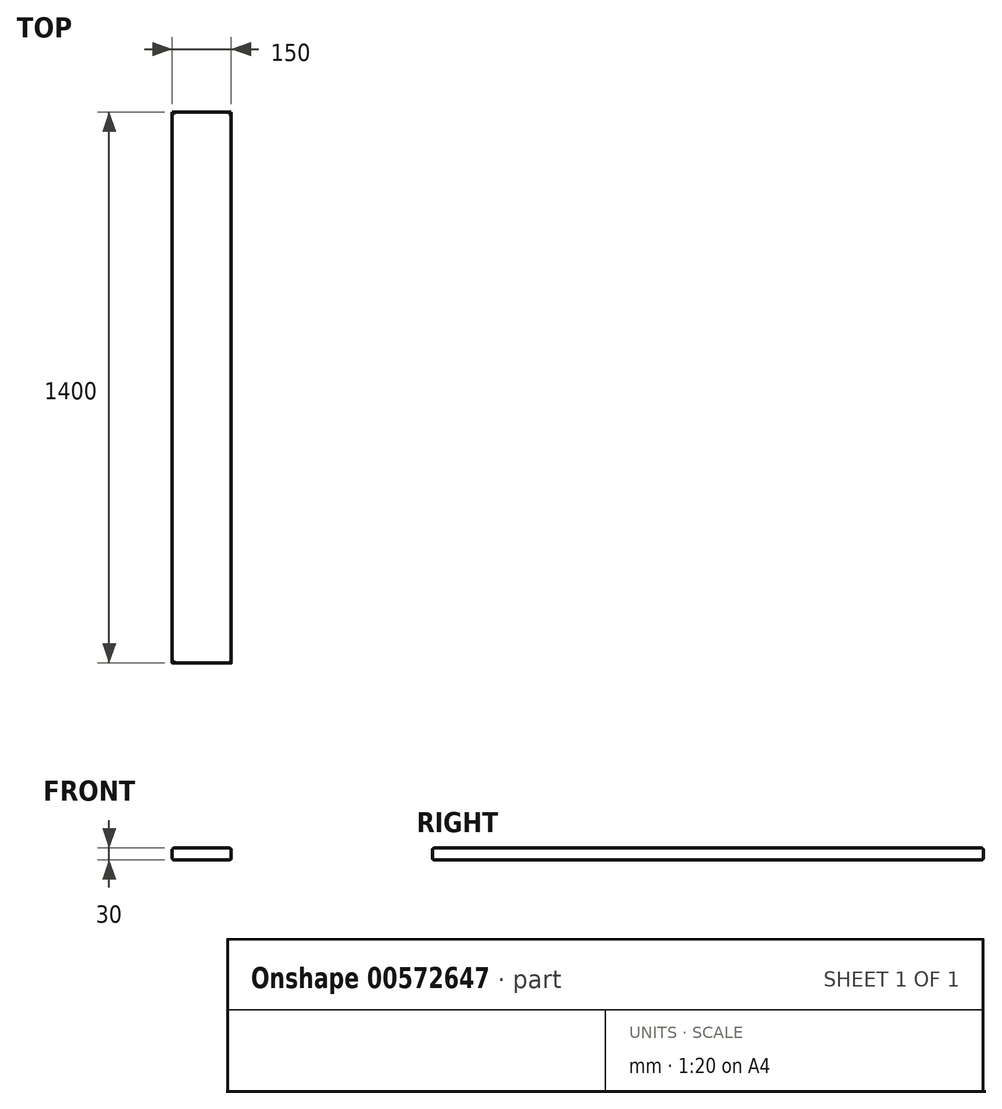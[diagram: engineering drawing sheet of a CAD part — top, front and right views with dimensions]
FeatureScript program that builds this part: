
annotation { "Feature Type Name" : "Feature", "Feature Type Description" : "" }
export const myFeature = defineFeature(function(context is Context, id is Id, definition is map)
    precondition{}
    {
        {
            var Q0;
            Q0=qCreatedBy(makeId("Front.planeOp"),FACE);
            var sketch = newSketch(context, id + "F0", { "sketchPlane" : qUnion([Q0])});
            skLineSegment(sketch, "E0.bottom", {"start": v(-76.63, -59.86) * mm, "end": v(73.37, -59.86) * mm});
            skLineSegment(sketch, "E0.top", {"start": v(-76.63, -89.86) * mm, "end": v(73.37, -89.86) * mm});
            skLineSegment(sketch, "E0.left", {"start": v(-76.63, -59.86) * mm, "end": v(-76.63, -89.86) * mm});
            skLineSegment(sketch, "E0.right", {"start": v(73.37, -59.86) * mm, "end": v(73.37, -89.86) * mm});
            skSolve(sketch);
        }
        {
            var Q0;
            Q0 = qSketchRegion(id + "F0", true);
            extrude(context, id + "F1", {"entities" : qUnion([Q0]), "depth" : 1400 * mm, "offsetDistance" : 25 * mm});
        }
        {
            var Q0;
            Q0=makeQuery(id+"F1.opExtrude","SWEPT_FACE",FACE,{"disambiguationData":[OSD([sQuery(id+"F0.wireOp",EDGE,"E0.bottom")])]});
            var Q1;
            Q1=makeQuery(id+"F1.opExtrude","SWEPT_FACE",FACE,{"disambiguationData":[OSD([sQuery(id+"F0.wireOp",EDGE,"E0.top")])]});
            fillet(context, id + "F2", {"entities" : qUnion([Q0, Q1]), "radius" : 5 * mm, "tangentPropagation" : true, "allowEdgeOverflow" : false});
        }
    });
